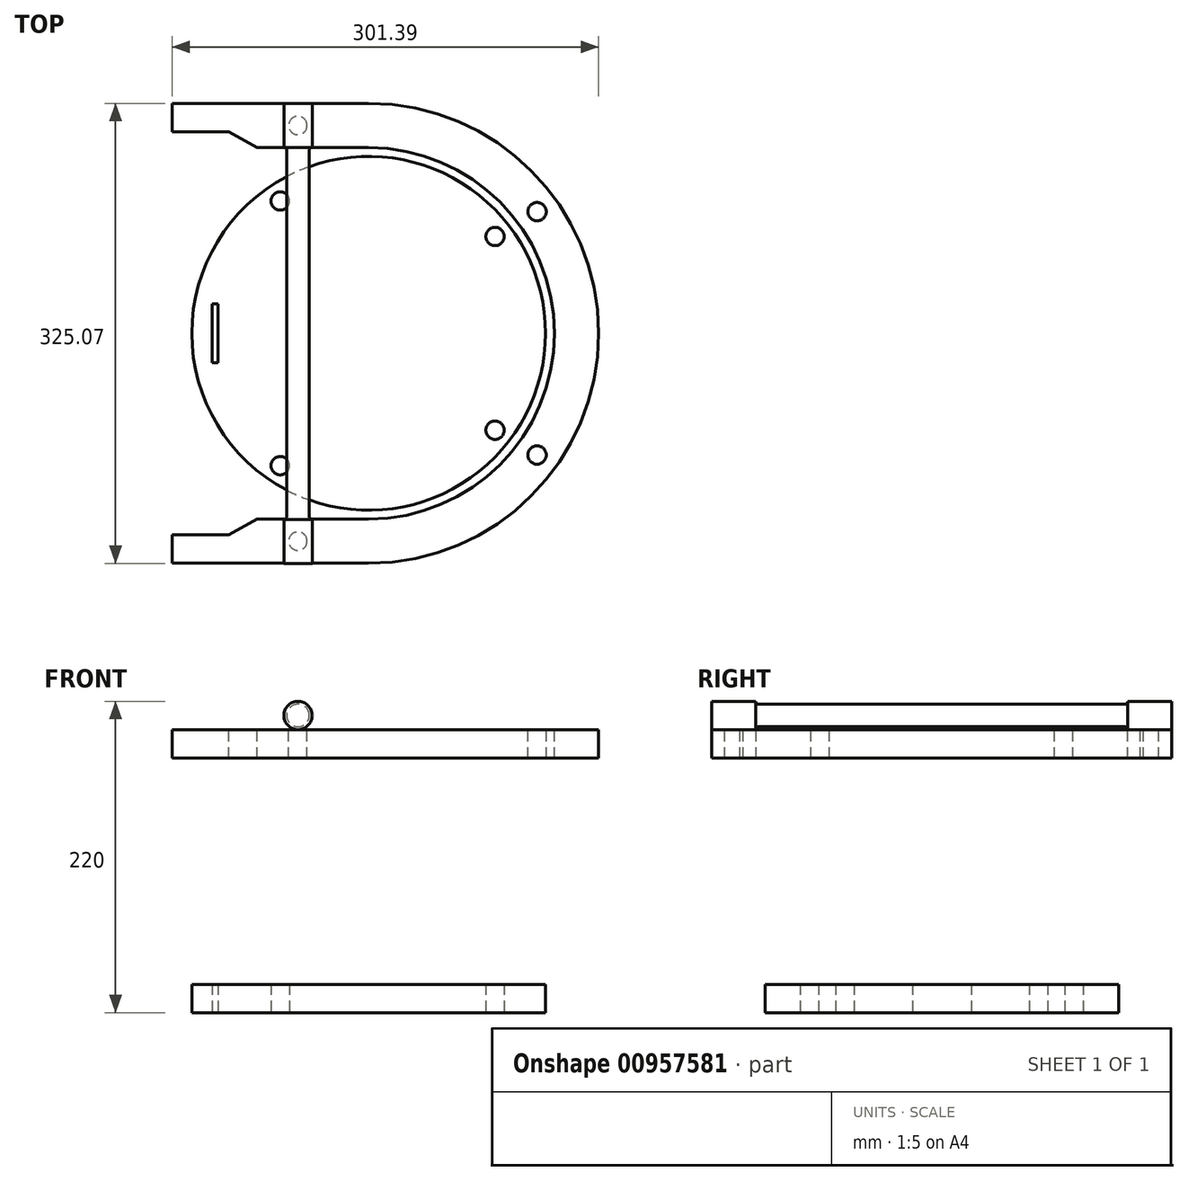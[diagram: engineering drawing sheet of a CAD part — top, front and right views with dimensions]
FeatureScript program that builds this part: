
annotation { "Feature Type Name" : "Feature", "Feature Type Description" : "" }
export const myFeature = defineFeature(function(context is Context, id is Id, definition is map)
    precondition{}
    {
        {
            var Q0;
            Q0=qCreatedBy(makeId("Top.planeOp"),FACE);
            var sketch = newSketch(context, id + "F0", { "sketchPlane" : qUnion([Q0])});
            skCircle(sketch, "E0", {"center": v(0, 0) * mm, "radius": 125 * mm});
            skCircle(sketch, "E1", {"center": v(0, 0) * mm, "radius": 112.5 * mm, "construction": true});
            skCircle(sketch, "E2", {"center": v(-62.5, 93.54) * mm, "radius": 6.5 * mm});
            skCircle(sketch, "E3", {"center": v(-62.5, -93.54) * mm, "radius": 6.5 * mm});
            skCircle(sketch, "E4", {"center": v(89.29, 68.44) * mm, "radius": 6.5 * mm});
            skCircle(sketch, "E5", {"center": v(89.29, -68.44) * mm, "radius": 6.5 * mm});
            skLineSegment(sketch, "E6.top", {"start": v(-106.55, 20.83) * mm, "end": v(-110.55, 20.83) * mm});
            skLineSegment(sketch, "E6.left", {"start": v(-106.55, 0) * mm, "end": v(-106.55, 20.83) * mm});
            skLineSegment(sketch, "E6.right", {"start": v(-110.55, 0) * mm, "end": v(-110.55, 20.83) * mm});
            skLineSegment(sketch, "E7.top", {"start": v(-106.55, -20.83) * mm, "end": v(-110.55, -20.83) * mm});
            skLineSegment(sketch, "E7.left", {"start": v(-106.55, 0) * mm, "end": v(-106.55, -20.83) * mm});
            skLineSegment(sketch, "E7.right", {"start": v(-110.55, 0) * mm, "end": v(-110.55, -20.83) * mm});
            skSolve(sketch);
        }
        {
            var Q0;
            Q0=makeQuery(id+"F0.imprint","IMPRINT",FACE,{"disambiguationData":[TD([[makeQuery(id+"F0.imprint","IMPRINT",EDGE,{"derivedFrom":sQuery(id+"F0.wireOp",EDGE,"E0")}),1.0]])]});
            extrude(context, id + "F1", {"entities" : qUnion([Q0]), "depth" : 20 * mm, "offsetDistance" : 25 * mm});
        }
        {
            var Q0;
            Q0=qCreatedBy(makeId("Top.planeOp"),FACE);
            cPlane(context, id + "F2", {"entities" : qUnion([Q0]), "cplaneType" : CPlaneType.OFFSET, "offset" : 200 * mm, "width" : 150 * mm, "height" : 150 * mm});
        }
        {
            var Q0;
            Q0=qCreatedBy(id+"F2.planeOp",FACE);
            var sketch = newSketch(context, id + "F3", { "sketchPlane" : qUnion([Q0])});
            skArc(sketch, "E8", {"start": v(0, -131.25) * mm, "mid": v(131.25, 0) * mm, "end": v(0, 131.25) * mm});
            skArc(sketch, "E9", {"start": v(0, -162.5) * mm, "mid": v(162.5, 0) * mm, "end": v(0, 162.5) * mm});
            skCircle(sketch, "E10", {"center": v(0, 0) * mm, "radius": 146.88 * mm, "construction": true});
            skCircle(sketch, "E11", {"center": v(119.05, 86.02) * mm, "radius": 6.5 * mm});
            skCircle(sketch, "E12", {"center": v(119.05, -86.02) * mm, "radius": 6.5 * mm});
            skLineSegment(sketch, "E13", {"start": v(0, 162.5) * mm, "end": v(-138.89, 162.5) * mm});
            skLineSegment(sketch, "E14", {"start": v(0, -162.5) * mm, "end": v(-138.89, -162.5) * mm});
            skLineSegment(sketch, "E15", {"start": v(-138.89, 162.5) * mm, "end": v(-138.89, 142.5) * mm, "construction": true});
            skLineSegment(sketch, "E16", {"start": v(-138.89, 130.6) * mm, "end": v(-138.89, 162.5) * mm, "construction": true});
            skLineSegment(sketch, "E17", {"start": v(-138.89, -162.5) * mm, "end": v(-138.89, -131.25) * mm, "construction": true});
            skLineSegment(sketch, "E18", {"start": v(-138.89, 142.5) * mm, "end": v(-98.89, 142.5) * mm});
            skLineSegment(sketch, "E19", {"start": v(-98.89, 142.5) * mm, "end": v(-78.89, 131.25) * mm});
            skLineSegment(sketch, "E20.trimOffspring", {"start": v(-138.89, 130.6) * mm, "end": v(-138.89, -131.25) * mm, "construction": true});
            skLineSegment(sketch, "E21", {"start": v(0, 146.88) * mm, "end": v(-199.91, 146.88) * mm, "construction": true});
            skLineSegment(sketch, "E22", {"start": v(0, -146.88) * mm, "end": v(-173.1, -146.88) * mm, "construction": true});
            skCircle(sketch, "E23", {"center": v(-50, 146.88) * mm, "radius": 6.5 * mm});
            skCircle(sketch, "E24", {"center": v(-50, -146.88) * mm, "radius": 6.5 * mm});
            skLineSegment(sketch, "E25", {"start": v(-78.89, 131.25) * mm, "end": v(0, 131.25) * mm});
            skLineSegment(sketch, "E26.MirrorCS", {"start": v(-78.89, -131.25) * mm, "end": v(0, -131.25) * mm});
            skLineSegment(sketch, "E27.MirrorCS", {"start": v(-98.89, -142.5) * mm, "end": v(-78.89, -131.25) * mm});
            skLineSegment(sketch, "E28.MirrorCS", {"start": v(-138.89, -142.5) * mm, "end": v(-98.89, -142.5) * mm});
            skLineSegment(sketch, "E29", {"start": v(-138.89, -162.5) * mm, "end": v(-138.89, -142.5) * mm});
            skLineSegment(sketch, "E30", {"start": v(-138.89, 142.5) * mm, "end": v(-138.89, 162.5) * mm});
            skSolve(sketch);
        }
        {
            var Q0;
            Q0=makeQuery(id+"F3.imprint","IMPRINT",FACE,{"disambiguationData":[TD([[makeQuery(id+"F3.imprint","IMPRINT",EDGE,{"derivedFrom":sQuery(id+"F3.wireOp",EDGE,"E8")}),-1.0]])]});
            extrude(context, id + "F4", {"entities" : qUnion([Q0]), "oppositeDirection" : true, "depth" : 20 * mm, "offsetDistance" : 25 * mm});
        }
        {
            var Q0;
            Q0=makeQuery(id+"F4.opExtrude","CAP_FACE",FACE,{"disambiguationData":[OSD([sQuery(id+"F3.wireOp",EDGE,"E8"),sQuery(id+"F3.wireOp",EDGE,"E9"),sQuery(id+"F3.wireOp",EDGE,"E11"),sQuery(id+"F3.wireOp",EDGE,"E12"),sQuery(id+"F3.wireOp",EDGE,"E13"),sQuery(id+"F3.wireOp",EDGE,"E14"),sQuery(id+"F3.wireOp",EDGE,"E18"),sQuery(id+"F3.wireOp",EDGE,"E19"),sQuery(id+"F3.wireOp",EDGE,"E23"),sQuery(id+"F3.wireOp",EDGE,"E24"),sQuery(id+"F3.wireOp",EDGE,"E25"),sQuery(id+"F3.wireOp",EDGE,"E26.MirrorCS"),sQuery(id+"F3.wireOp",EDGE,"E27.MirrorCS"),sQuery(id+"F3.wireOp",EDGE,"E28.MirrorCS"),sQuery(id+"F3.wireOp",EDGE,"E29"),sQuery(id+"F3.wireOp",EDGE,"E30")])],"isStart":true});
            cPlane(context, id + "F5", {"entities" : qUnion([Q0]), "cplaneType" : CPlaneType.OFFSET, "offset" : 10 * mm, "width" : 150 * mm, "height" : 150 * mm});
        }
        {
            var Q0;
            Q0=qCreatedBy(id+"F5.planeOp",FACE);
            var sketch = newSketch(context, id + "F6", { "sketchPlane" : qUnion([Q0])});
            skLineSegment(sketch, "E31", {"start": v(-49.94, 162.43) * mm, "end": v(-49.94, -175.43) * mm, "construction": true});
            skLineSegment(sketch, "E32", {"start": v(-49.94, -162.57) * mm, "end": v(-59.94, -162.57) * mm});
            skLineSegment(sketch, "E33", {"start": v(-59.94, -162.57) * mm, "end": v(-59.94, -131.57) * mm});
            skLineSegment(sketch, "E34", {"start": v(-59.94, -131.57) * mm, "end": v(-59.94, -131.57) * mm});
            skLineSegment(sketch, "E35", {"start": v(-57.94, -129.57) * mm, "end": v(-57.94, 129.43) * mm});
            skLineSegment(sketch, "E36", {"start": v(-59.94, 131.43) * mm, "end": v(-59.94, 131.43) * mm});
            skLineSegment(sketch, "E37", {"start": v(-59.94, 131.43) * mm, "end": v(-59.94, 162.43) * mm});
            skLineSegment(sketch, "E38", {"start": v(-59.94, 162.43) * mm, "end": v(-49.94, 162.43) * mm});
            skPoint(sketch, "E39.visualSharp", {"position": v(-57.94, 131.43) * mm});
            skArc(sketch, "E39.filletArc", {"start": v(-57.94, 129.43) * mm, "mid": v(-58.53, 130.84) * mm, "end": v(-59.94, 131.43) * mm});
            skPoint(sketch, "E40.visualSharp", {"position": v(-57.94, -131.57) * mm});
            skArc(sketch, "E40.filletArc", {"start": v(-59.94, -131.57) * mm, "mid": v(-58.53, -130.99) * mm, "end": v(-57.94, -129.57) * mm});
            skLineSegment(sketch, "E41", {"start": v(-49.94, 162.43) * mm, "end": v(-49.94, -162.57) * mm});
            skSolve(sketch);
        }
        {
            var Q0;
            Q0 = qSketchRegion(id + "F6", true);
            var Q1;
            Q1=sQuery(id+"F6.wireOp",EDGE,"E41");
            revolve(context, id + "F7", {"operationType" : NewBodyOperationType.ADD, "surfaceOperationType" : NewSurfaceOperationType.NEW, "entities" : qUnion([Q0]), "axis" : qUnion([Q1]), "revolveType" : RevolveType.FULL});
        }
    });
